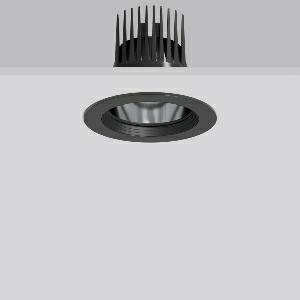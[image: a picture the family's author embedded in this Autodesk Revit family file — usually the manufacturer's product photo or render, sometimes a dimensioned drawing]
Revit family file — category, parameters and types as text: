
# Revit family: heledon_maxi_e_901770_003_76_685e
name_source: partatom
category: Lighting Fixtures
units: mm (PartAtom-declared; Revit-internal decimal feet)

## family parameters
Cut with Voids When Loaded = No
Host = Face
Light Source = No
Part Type = Normal
Room Calculation Point = No
Round Connector Dimension = Use Diameter
Shared = No

## types (1)
- HELEDON maxi E (1 x LED Modul 932 fresh meat, 2100 lm, 3200)
    Apparent Load = 33 VA
    Approval mark = CE
    CIE Flux Codes = 100 100 100 100 100
    Color Rendering = 90
    Color Temperature = 3200
    Default Elevation = 1800 mm
    Description = Series: HELEDON maxi
Round recessed downlight. Housing: die-cast aluminium, powder-coated. Black plastic ring and recessed LED to prevent glare from the side. Optical assembly with reflector made of MIRO-Silver with 98% total light reflection for outstanding efficiency - can be changed without tools. Special LED for illumination of meat included. Suitable for Recessed ceiling mounting. Installation without tools thanks to spring fastening system. Including separate LED converter with connecting cable 600 mm.High quality converter without flickering and stroboscopic effect. Through-wiring box (5 pole) available as accessory. The following accessories can be mounted without use of tools: interchangeable lenses, decorative glasses, honeycomb louvre, clear and frosted diffusers, white interchangeable plastic ring. 
Colour: deep black, matt (RAL 9005)
Diameter: 162 mm
Height: 3 mm
Cut-out diameter: 152 mm
Recess height: 200 mm
Luminaire: recess height: 135 mm
Lamp: LED
Socket: without socket
Colour temperature: fresh meat
System power: 33 W
Rated luminous flux: 2100 lm
Luminous efficiency: 64 lm/W
Control gear: Converter, dimmable, DALI
Protection class: II
Type of protection: IP 20
    Height = 0 mm  [stored 0 ft]
    Lamp = 1 x LED Modul 932 fresh meat
    Lamp Light Flux = 2100 lm
    Lamp count = 1
    Length = 162 mm
    Lifetime = 50000 h
    Luminous efficacy = 64 lm/W
    Manufacturer = RZB
    ModVariant = No
    Model = 901770.003.76
    Mounting Place = Ceiling
    Mounting Type = Recessed
    Number of Poles = 1
    OnlyDefault = Yes
    Power Factor = 1
    Product Name = HELEDON maxi E
    Product group = Recessed downlights
    ProductGroupID = 402
    Protection Class = Protection class II
    Protection Degree = IP 20
    RLX_Detail_Level = 1
    RLX_Emergency_Light_Flux = 0 lm
    RLX_Emergency_Type = 0
    RLX_Emergency_Type_DB = No
    RlxData = <blob elided: 122745 chars, md5=8dbdb201>
    Socket = socket
    Standby Power = 0 W
    System Light Flux = 2100 lm
    System Power = 33 W
    Type Comments = Product without accessories
    Type Image = 901662.003.jpg
    URL = http://relux.com
    VarID = ---
    Voltage = 230 V
    Voltage Range = 220-240 V
    Weight = 0.00 kg
    Width = 0 mm  [stored 0 ft]

note: [stored X ft] marks values corroborated as IEEE doubles in the binary element streams (Revit-internal decimal feet)

## geometry (parser evidence)
native form markers: Blend x4, Sweep x12
no freeform markers — native parametric forms only
